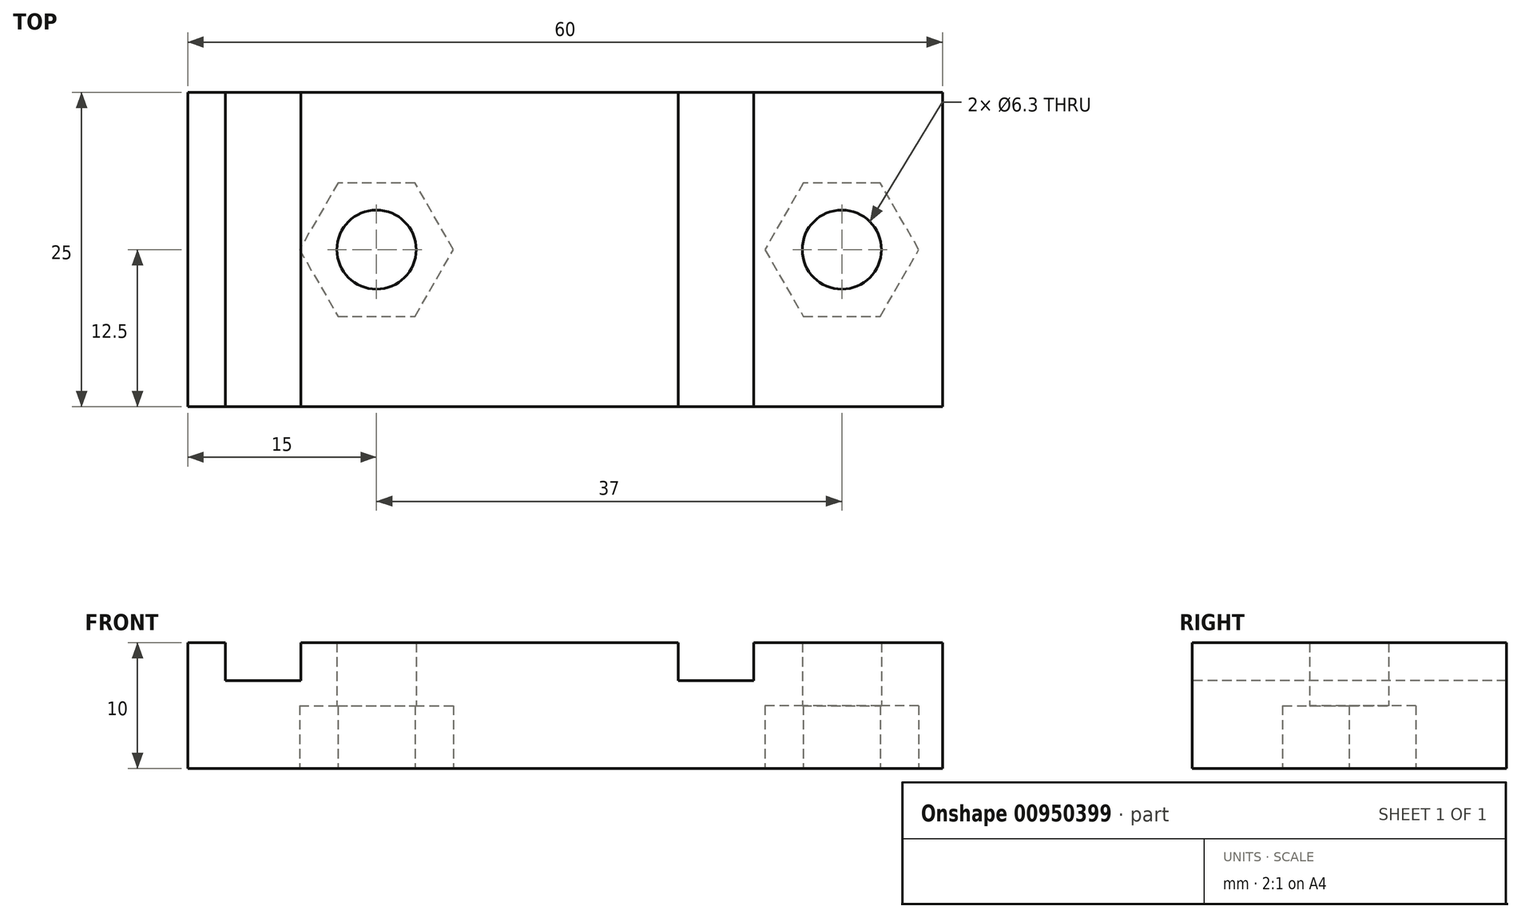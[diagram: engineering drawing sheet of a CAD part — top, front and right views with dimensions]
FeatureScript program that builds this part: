
annotation { "Feature Type Name" : "Feature", "Feature Type Description" : "" }
export const myFeature = defineFeature(function(context is Context, id is Id, definition is map)
    precondition{}
    {
        {
            var Q0;
            Q0=qCreatedBy(makeId("Top.planeOp"),FACE);
            var sketch = newSketch(context, id + "F0", { "sketchPlane" : qUnion([Q0])});
            skLineSegment(sketch, "E0.bottom", {"start": v(0, 0) * mm, "end": v(60, 0) * mm});
            skLineSegment(sketch, "E0.top", {"start": v(0, 25) * mm, "end": v(60, 25) * mm});
            skLineSegment(sketch, "E0.left", {"start": v(0, 0) * mm, "end": v(0, 25) * mm});
            skLineSegment(sketch, "E0.right", {"start": v(60, 0) * mm, "end": v(60, 25) * mm});
            skSolve(sketch);
        }
        {
            var Q0;
            Q0=makeQuery(id+"F0.imprint","IMPRINT",FACE,{"disambiguationData":[TD([[makeQuery(id+"F0.imprint","IMPRINT",EDGE,{"derivedFrom":sQuery(id+"F0.wireOp",EDGE,"E0.bottom")}),1.0]])]});
            extrude(context, id + "F1", {"entities" : qUnion([Q0]), "depth" : 10 * mm, "offsetDistance" : 25 * mm});
        }
        {
            var Q0;
            Q0=makeQuery(id+"F1.opExtrude","CAP_FACE",FACE,{"disambiguationData":[OSD([sQuery(id+"F0.wireOp",EDGE,"E0.bottom"),sQuery(id+"F0.wireOp",EDGE,"E0.top"),sQuery(id+"F0.wireOp",EDGE,"E0.left"),sQuery(id+"F0.wireOp",EDGE,"E0.right")])],"isStart":false});
            var sketch = newSketch(context, id + "F2", { "sketchPlane" : qUnion([Q0])});
            skLineSegment(sketch, "E1.bottom", {"start": v(3, 25) * mm, "end": v(9, 25) * mm});
            skLineSegment(sketch, "E1.top", {"start": v(3, 0) * mm, "end": v(9, 0) * mm});
            skLineSegment(sketch, "E1.left", {"start": v(3, 25) * mm, "end": v(3, 0) * mm});
            skLineSegment(sketch, "E1.right", {"start": v(9, 25) * mm, "end": v(9, 0) * mm});
            skLineSegment(sketch, "E2.bottom", {"start": v(39, 25) * mm, "end": v(45, 25) * mm});
            skLineSegment(sketch, "E2.top", {"start": v(39, 0) * mm, "end": v(45, 0) * mm});
            skLineSegment(sketch, "E2.left", {"start": v(39, 25) * mm, "end": v(39, 0) * mm});
            skLineSegment(sketch, "E2.right", {"start": v(45, 25) * mm, "end": v(45, 0) * mm});
            skSolve(sketch);
        }
        {
            var Q0;
            Q0 = qSketchRegion(id + "F2", true);
            extrude(context, id + "F3", {"entities" : qUnion([Q0]), "operationType" : NewBodyOperationType.REMOVE, "oppositeDirection" : true, "depth" : 3 * mm, "offsetDistance" : 25 * mm});
        }
        {
            var Q0;
            Q0=makeQuery(id+"F1.opExtrude","CAP_FACE",FACE,{"disambiguationData":[OSD([sQuery(id+"F0.wireOp",EDGE,"E0.bottom"),sQuery(id+"F0.wireOp",EDGE,"E0.top"),sQuery(id+"F0.wireOp",EDGE,"E0.left"),sQuery(id+"F0.wireOp",EDGE,"E0.right")])],"isStart":true});
            var sketch = newSketch(context, id + "F4", { "sketchPlane" : qUnion([Q0])});
            skPoint(sketch, "E3", {"position": v(15, -12.5) * mm});
            skPoint(sketch, "E4", {"position": v(52, -12.5) * mm});
            skSolve(sketch);
        }
        {
            var Q0;
            Q0=makeQuery(id+"F4.imprint","IMPRINT",FACE,{"disambiguationData":[TD([[makeQuery(id+"F4.imprint","IMPRINT",EDGE,{"derivedFrom":makeQuery(id+"F1.opExtrude","CAP_EDGE",EDGE,{"disambiguationData":[OSD([sQuery(id+"F0.wireOp",EDGE,"E0.bottom")])],"isStart":true})}),-1.0]])]});
            var sketch = newSketch(context, id + "F5", { "sketchPlane" : qUnion([Q0])});
            skCircle(sketch, "E5.cCircle", {"center": v(15, -12.5) * mm, "radius": 5.3 * mm, "construction": true});
            skLineSegment(sketch, "E5.0", {"start": v(18.06, -7.2) * mm, "end": v(21.12, -12.5) * mm});
            skLineSegment(sketch, "E5.1", {"start": v(21.12, -12.5) * mm, "end": v(18.06, -17.8) * mm});
            skLineSegment(sketch, "E5.2", {"start": v(18.06, -17.8) * mm, "end": v(11.94, -17.8) * mm});
            skLineSegment(sketch, "E5.3", {"start": v(11.94, -17.8) * mm, "end": v(8.88, -12.5) * mm});
            skLineSegment(sketch, "E5.4", {"start": v(8.88, -12.5) * mm, "end": v(11.94, -7.2) * mm});
            skLineSegment(sketch, "E5.5", {"start": v(11.94, -7.2) * mm, "end": v(18.06, -7.2) * mm});
            skPoint(sketch, "E5.0.midPoint", {"position": v(19.59, -9.85) * mm});
            skLineSegment(sketch, "E6.1.0.0", {"start": v(48.94, -17.8) * mm, "end": v(45.88, -12.5) * mm});
            skLineSegment(sketch, "E6.1.0.1", {"start": v(45.88, -12.5) * mm, "end": v(48.94, -7.2) * mm});
            skPoint(sketch, "E6.1.0.2", {"position": v(56.59, -9.85) * mm});
            skLineSegment(sketch, "E6.1.0.3", {"start": v(55.06, -17.8) * mm, "end": v(48.94, -17.8) * mm});
            skLineSegment(sketch, "E6.1.0.4", {"start": v(58.12, -12.5) * mm, "end": v(55.06, -17.8) * mm});
            skCircle(sketch, "E6.1.0.5", {"center": v(52, -12.5) * mm, "radius": 5.3 * mm, "construction": true});
            skLineSegment(sketch, "E6.1.0.6", {"start": v(48.94, -7.2) * mm, "end": v(55.06, -7.2) * mm});
            skLineSegment(sketch, "E6.1.0.7", {"start": v(55.06, -7.2) * mm, "end": v(58.12, -12.5) * mm});
            skLineSegment(sketch, "E6.direction1", {"start": v(11.94, -17.8) * mm, "end": v(48.94, -17.8) * mm, "construction": true});
            skSolve(sketch);
        }
        {
            var Q0;
            Q0=sQuery(id+"F4.wireOp",VERTEX,"E3");
            var Q1;
            Q1=sQuery(id+"F4.wireOp",VERTEX,"E4");
            var Q2;
            Q2=makeQuery(id+"F1.opExtrude","SWEPT_BODY",BODY,{"disambiguationData":[OSD([sQuery(id+"F0.wireOp",EDGE,"E0.bottom"),sQuery(id+"F0.wireOp",EDGE,"E0.top"),sQuery(id+"F0.wireOp",EDGE,"E0.left"),sQuery(id+"F0.wireOp",EDGE,"E0.right")])]});
            hole(context, id + "F6", {"style" : HoleStyle.SIMPLE, "endStyle" : HoleEndStyle.THROUGH, "holeDiameter" : 6.3 * mm, "majorDiameter" : 5 * mm, "tappedDepth" : 12 * mm, "tapClearance" : 3, "locations" : qUnion([Q0, Q1]), "scope" : qUnion([Q2])});
        }
        {
            var Q0;
            Q0 = qSketchRegion(id + "F5", true);
            extrude(context, id + "F7", {"entities" : qUnion([Q0]), "operationType" : NewBodyOperationType.REMOVE, "oppositeDirection" : true, "depth" : 5 * mm, "offsetDistance" : 25 * mm});
        }
    });
